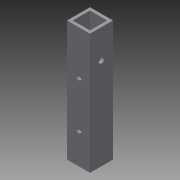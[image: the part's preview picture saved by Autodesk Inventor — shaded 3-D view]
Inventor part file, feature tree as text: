
AUTODESK INVENTOR PART (.ipt)
format: ipt  version: 2013 (Build 170138000, 138)  size: 100,352 bytes
history: native  units: in
note: dims shown in document units (in); Inventor stores cm internally (conversion verified against a paired STEP export)
features: extrude x3, sketch x3
ambient origin geometry x8: Origin, YZ Plane, XZ Plane, XY Plane, X Axis, Y Axis, Z Axis, Center Point
bodies: Solid1 (feature_tree)
feature tree (6):
  extrude  "Extrusion1"  Depth=5.25in
  extrude  "Extrusion2"  Depth=3.625in
  extrude  "Extrusion3"  TaperAngle=90.0deg  [1 undecoded]
  sketch  "Sketch1"  dims[d0=1.0in d1=5.25in]
  sketch  "Sketch2"  dims[d2=1.0in d3=3.625in]
  sketch  "Sketch3"  dims[d4=3.375in d5=90.0deg d6=0.25in d7=2.0in d8=0.25in d9=1.0in d10=0.0in d11=0.75in d12=0.75in d13=10.0in d14=0.0in d15=1.25in d16=90.0deg d17=0.25in d18=10.0in d19=0.0in]
note: 1 required parameter value undecoded (feature->parameter linkage not recoverable at this tier; creation-order binding heuristic only, values carry confidence <= 0.55)
